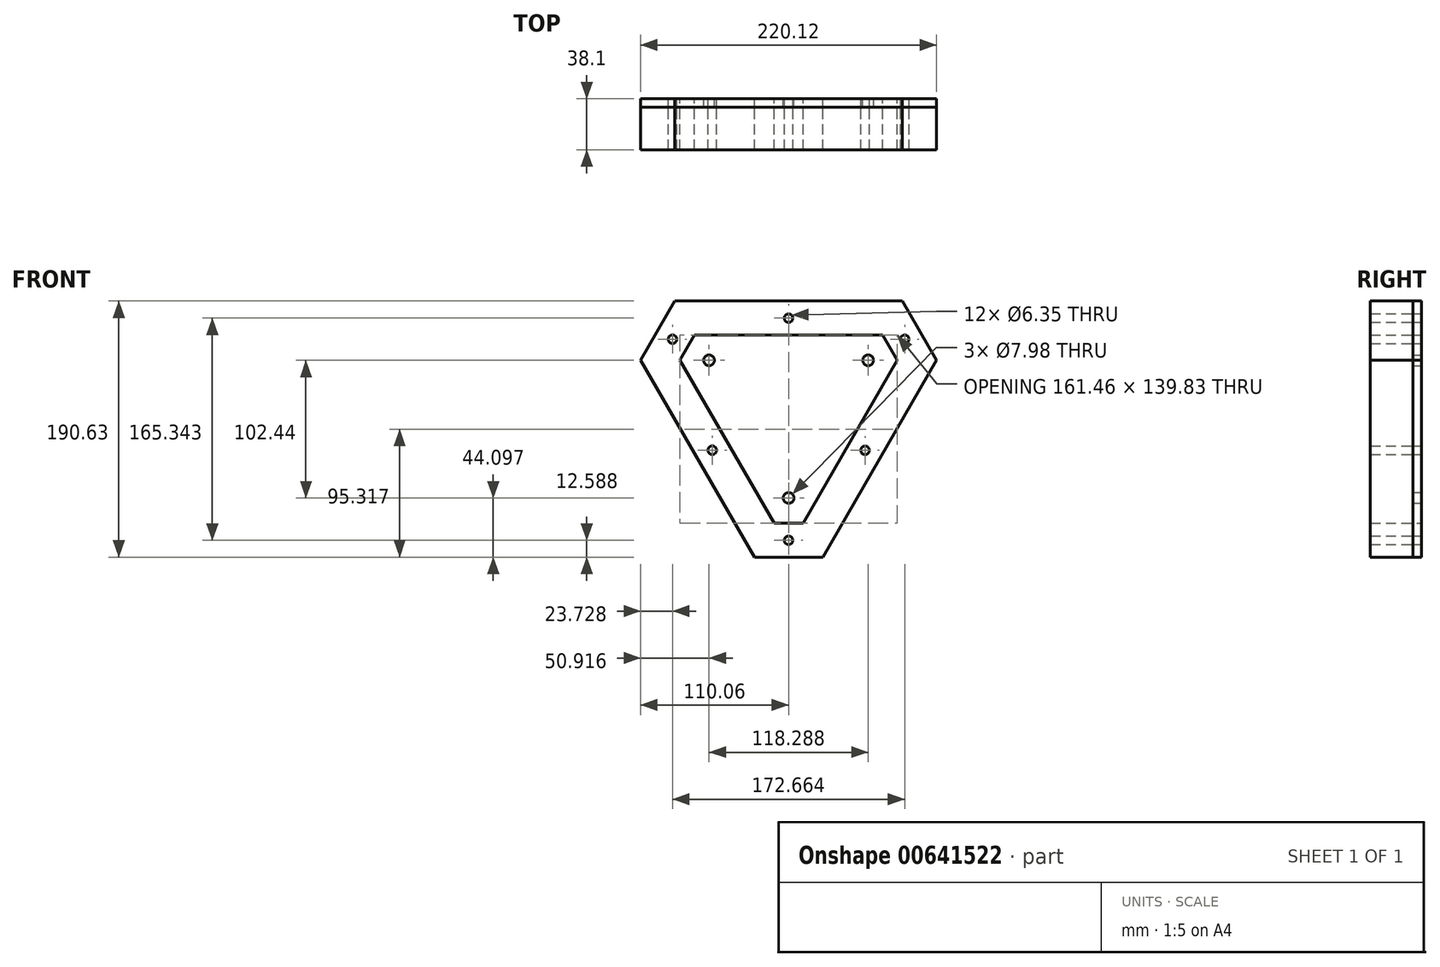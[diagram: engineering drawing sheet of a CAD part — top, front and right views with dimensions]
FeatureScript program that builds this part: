
annotation { "Feature Type Name" : "Feature", "Feature Type Description" : "" }
export const myFeature = defineFeature(function(context is Context, id is Id, definition is map)
    precondition{}
    {
        {
            var Q0;
            Q0=qCreatedBy(makeId("Front.planeOp"),FACE);
            var sketch = newSketch(context, id + "F0", { "sketchPlane" : qUnion([Q0])});
            skCircle(sketch, "E0.cCircle", {"center": v(0, 0) * mm, "radius": 68.3 * mm, "construction": true});
            skLineSegment(sketch, "E0.0", {"start": v(59.14, 34.15) * mm, "end": v(0, -68.3) * mm, "construction": true});
            skLineSegment(sketch, "E0.1", {"start": v(0, -68.3) * mm, "end": v(-59.14, 34.15) * mm, "construction": true});
            skLineSegment(sketch, "E0.2", {"start": v(-59.14, 34.15) * mm, "end": v(59.14, 34.15) * mm, "construction": true});
            skArc(sketch, "E1", {"start": v(-61.91, 28.83) * mm, "mid": v(-53.95, 31.15) * mm, "end": v(-55.92, 39.2) * mm, "construction": true});
            skArc(sketch, "E2", {"start": v(55.92, 39.2) * mm, "mid": v(53.95, 31.15) * mm, "end": v(61.91, 28.83) * mm, "construction": true});
            skArc(sketch, "E3", {"start": v(-5.2, -71.3) * mm, "mid": v(0, -74.29) * mm, "end": v(5.2, -71.3) * mm});
            skLineSegment(sketch, "E4", {"start": v(-59.14, 40.14) * mm, "end": v(59.14, 40.14) * mm});
            skLineSegment(sketch, "E5", {"start": v(64.34, 31.15) * mm, "end": v(5.2, -71.3) * mm});
            skLineSegment(sketch, "E6", {"start": v(-64.34, 31.15) * mm, "end": v(-5.2, -71.3) * mm});
            skArc(sketch, "E7.trimOffspring", {"start": v(-59.14, 40.14) * mm, "mid": v(-64.34, 37.14) * mm, "end": v(-64.34, 31.15) * mm});
            skArc(sketch, "E8.trimOffspring", {"start": v(64.34, 31.15) * mm, "mid": v(64.34, 37.14) * mm, "end": v(59.14, 40.14) * mm});
            skArc(sketch, "E9.trimOffspring", {"start": v(5.99, -68.03) * mm, "mid": v(0, -62.3) * mm, "end": v(-5.99, -68.03) * mm, "construction": true});
            skLineSegment(sketch, "E10", {"start": v(-69.94, 52.84) * mm, "end": v(69.94, 52.84) * mm});
            skLineSegment(sketch, "E11", {"start": v(80.73, 34.15) * mm, "end": v(69.94, 52.84) * mm});
            skLineSegment(sketch, "E12", {"start": v(10.8, -86.99) * mm, "end": v(-10.8, -86.99) * mm});
            skLineSegment(sketch, "E13", {"start": v(-10.8, -86.99) * mm, "end": v(-80.73, 34.15) * mm});
            skLineSegment(sketch, "E14", {"start": v(-69.94, 52.84) * mm, "end": v(-80.73, 34.15) * mm});
            skLineSegment(sketch, "E15", {"start": v(10.8, -86.99) * mm, "end": v(80.73, 34.15) * mm});
            skLineSegment(sketch, "E16", {"start": v(0, 52.84) * mm, "end": v(0, 78.24) * mm, "construction": true});
            skPoint(sketch, "E16.endSnap0", {"position": v(0, 52.84) * mm});
            skLineSegment(sketch, "E17", {"start": v(-45.76, -26.42) * mm, "end": v(-67.76, -39.12) * mm, "construction": true});
            skLineSegment(sketch, "E18", {"start": v(45.76, -26.42) * mm, "end": v(67.76, -39.12) * mm, "construction": true});
            skLineSegment(sketch, "E19", {"start": v(67.76, -39.12) * mm, "end": v(110.06, 34.15) * mm, "construction": true});
            skLineSegment(sketch, "E20", {"start": v(-110.06, 34.15) * mm, "end": v(-25.2, -112.39) * mm, "construction": true});
            skLineSegment(sketch, "E21", {"start": v(-84.6, 78.24) * mm, "end": v(84.6, 78.24) * mm, "construction": true});
            skLineSegment(sketch, "E22", {"start": v(67.76, -39.12) * mm, "end": v(25.46, -112.39) * mm, "construction": true});
            skLineSegment(sketch, "E23", {"start": v(0, -86.99) * mm, "end": v(0, -112.39) * mm, "construction": true});
            skLineSegment(sketch, "E24", {"start": v(0, -112.39) * mm, "end": v(-25.2, -112.39) * mm, "construction": true});
            skLineSegment(sketch, "E25", {"start": v(0, -112.39) * mm, "end": v(25.46, -112.39) * mm, "construction": true});
            skLineSegment(sketch, "E26", {"start": v(-25.2, -112.39) * mm, "end": v(-10.8, -86.99) * mm, "construction": true});
            skLineSegment(sketch, "E27", {"start": v(25.46, -112.39) * mm, "end": v(10.8, -86.99) * mm, "construction": true});
            skLineSegment(sketch, "E28", {"start": v(-75.33, 43.5) * mm, "end": v(-97.33, 56.2) * mm, "construction": true});
            skLineSegment(sketch, "E29", {"start": v(-97.33, 56.2) * mm, "end": v(-110.06, 34.15) * mm, "construction": true});
            skLineSegment(sketch, "E30", {"start": v(-97.33, 56.2) * mm, "end": v(-84.6, 78.24) * mm, "construction": true});
            skLineSegment(sketch, "E31", {"start": v(-80.73, 34.15) * mm, "end": v(-110.06, 34.15) * mm, "construction": true});
            skLineSegment(sketch, "E32", {"start": v(-69.94, 52.84) * mm, "end": v(-84.6, 78.24) * mm, "construction": true});
            skLineSegment(sketch, "E33", {"start": v(75.33, 43.5) * mm, "end": v(97.33, 56.2) * mm, "construction": true});
            skLineSegment(sketch, "E34", {"start": v(97.33, 56.2) * mm, "end": v(84.6, 78.24) * mm, "construction": true});
            skLineSegment(sketch, "E35", {"start": v(97.33, 56.2) * mm, "end": v(110.06, 34.15) * mm, "construction": true});
            skLineSegment(sketch, "E36", {"start": v(69.94, 52.84) * mm, "end": v(84.6, 78.24) * mm, "construction": true});
            skLineSegment(sketch, "E37", {"start": v(80.73, 34.15) * mm, "end": v(110.06, 34.15) * mm, "construction": true});
            skLineSegment(sketch, "E38", {"start": v(-110.06, 34.15) * mm, "end": v(-110.06, 78.24) * mm, "construction": true});
            skLineSegment(sketch, "E39", {"start": v(-110.06, 34.15) * mm, "end": v(-110.06, -112.39) * mm, "construction": true});
            skLineSegment(sketch, "E40", {"start": v(-84.6, 78.24) * mm, "end": v(-110.06, 78.24) * mm, "construction": true});
            skLineSegment(sketch, "E41", {"start": v(-25.2, -112.39) * mm, "end": v(-110.06, -112.39) * mm, "construction": true});
            skLineSegment(sketch, "E42", {"start": v(110.06, 34.15) * mm, "end": v(110.06, 78.24) * mm, "construction": true});
            skLineSegment(sketch, "E43", {"start": v(84.6, 78.24) * mm, "end": v(110.06, 78.24) * mm, "construction": true});
            skLineSegment(sketch, "E44", {"start": v(110.06, 34.15) * mm, "end": v(110.06, -112.39) * mm, "construction": true});
            skLineSegment(sketch, "E45", {"start": v(25.46, -112.39) * mm, "end": v(110.06, -112.39) * mm, "construction": true});
            skLineSegment(sketch, "E46", {"start": v(-110.06, 78.24) * mm, "end": v(110.06, 78.24) * mm});
            skLineSegment(sketch, "E47", {"start": v(110.06, -112.39) * mm, "end": v(110.06, 78.24) * mm});
            skLineSegment(sketch, "E48", {"start": v(110.06, -112.39) * mm, "end": v(-110.06, -112.39) * mm});
            skLineSegment(sketch, "E49", {"start": v(-110.06, -112.39) * mm, "end": v(-110.06, 78.24) * mm});
            skCircle(sketch, "E50", {"center": v(0, -68.3) * mm, "radius": 3.99 * mm});
            skCircle(sketch, "E51", {"center": v(59.14, 34.15) * mm, "radius": 3.99 * mm});
            skCircle(sketch, "E52", {"center": v(-59.14, 34.15) * mm, "radius": 3.99 * mm});
            skLineSegment(sketch, "E53", {"start": v(-84.6, 78.24) * mm, "end": v(-110.06, 34.15) * mm});
            skLineSegment(sketch, "E54", {"start": v(-110.06, 34.15) * mm, "end": v(-25.2, -112.39) * mm});
            skLineSegment(sketch, "E55", {"start": v(25.46, -112.39) * mm, "end": v(110.06, 34.15) * mm});
            skLineSegment(sketch, "E56", {"start": v(110.06, 34.15) * mm, "end": v(84.6, 78.24) * mm});
            skLineSegment(sketch, "E57", {"start": v(25.46, -112.39) * mm, "end": v(10.8, -86.99) * mm});
            skLineSegment(sketch, "E58", {"start": v(-10.8, -86.99) * mm, "end": v(-25.2, -112.39) * mm});
            skLineSegment(sketch, "E59", {"start": v(80.73, 34.15) * mm, "end": v(110.06, 34.15) * mm});
            skLineSegment(sketch, "E60", {"start": v(69.94, 52.84) * mm, "end": v(84.6, 78.24) * mm});
            skLineSegment(sketch, "E61", {"start": v(-69.94, 52.84) * mm, "end": v(-84.6, 78.24) * mm});
            skLineSegment(sketch, "E62", {"start": v(-80.73, 34.15) * mm, "end": v(-110.06, 34.15) * mm});
            skLineSegment(sketch, "E63", {"start": v(0, 65.54) * mm, "end": v(-77.27, 65.54) * mm, "construction": true});
            skLineSegment(sketch, "E64", {"start": v(-77.27, 65.54) * mm, "end": v(-95.4, 34.15) * mm, "construction": true});
            skLineSegment(sketch, "E65", {"start": v(-95.4, 34.15) * mm, "end": v(-56.76, -32.77) * mm, "construction": true});
            skLineSegment(sketch, "E66", {"start": v(-56.76, -32.77) * mm, "end": v(-18.06, -99.8) * mm, "construction": true});
            skLineSegment(sketch, "E67", {"start": v(-18.06, -99.8) * mm, "end": v(18.2, -99.8) * mm, "construction": true});
            skLineSegment(sketch, "E68", {"start": v(18.2, -99.8) * mm, "end": v(56.86, -32.83) * mm, "construction": true});
            skLineSegment(sketch, "E69", {"start": v(56.86, -32.83) * mm, "end": v(94.84, 34.15) * mm, "construction": true});
            skPoint(sketch, "E70.endSnap0", {"position": v(77.27, 65.54) * mm});
            skLineSegment(sketch, "E71", {"start": v(77.27, 65.54) * mm, "end": v(0, 65.54) * mm, "construction": true});
            skLineSegment(sketch, "E72", {"start": v(77.27, 65.54) * mm, "end": v(86.33, 49.84) * mm, "construction": true});
            skLineSegment(sketch, "E73", {"start": v(86.33, 49.84) * mm, "end": v(94.84, 34.15) * mm, "construction": true});
            skCircle(sketch, "E74", {"center": v(-56.76, -32.77) * mm, "radius": 3.18 * mm});
            skCircle(sketch, "E75", {"center": v(56.86, -32.83) * mm, "radius": 3.18 * mm});
            skCircle(sketch, "E76", {"center": v(0, -99.8) * mm, "radius": 3.18 * mm});
            skCircle(sketch, "E77", {"center": v(0, 65.54) * mm, "radius": 3.18 * mm});
            skCircle(sketch, "E78", {"center": v(-86.33, 49.84) * mm, "radius": 3.18 * mm});
            skCircle(sketch, "E79", {"center": v(86.33, 49.84) * mm, "radius": 3.18 * mm});
            skSolve(sketch);
        }
        {
            var Q0;
            Q0=makeQuery(id+"F0.imprint","IMPRINT",FACE,{"disambiguationData":[TD([[makeQuery(id+"F0.imprint","IMPRINT",EDGE,{"derivedFrom":sQuery(id+"F0.wireOp",EDGE,"E3")}),-1.0]])]});
            var Q1;
            Q1=makeQuery(id+"F0.imprint","IMPRINT",FACE,{"disambiguationData":[TD([[makeQuery(id+"F0.imprint","IMPRINT",EDGE,{"derivedFrom":sQuery(id+"F0.wireOp",EDGE,"E3")}),1.0]])]});
            var Q2;
            Q2=makeQuery(id+"F0.imprint","IMPRINT",FACE,{"disambiguationData":[TD([[makeQuery(id+"F0.imprint","IMPRINT",EDGE,{"derivedFrom":sQuery(id+"F0.wireOp",EDGE,"E14")}),-1.0]])]});
            var Q3;
            Q3=makeQuery(id+"F0.imprint","IMPRINT",FACE,{"disambiguationData":[TD([[makeQuery(id+"F0.imprint","IMPRINT",EDGE,{"derivedFrom":sQuery(id+"F0.wireOp",EDGE,"E13")}),1.0]])]});
            var Q4;
            Q4=makeQuery(id+"F0.imprint","IMPRINT",FACE,{"disambiguationData":[TD([[makeQuery(id+"F0.imprint","IMPRINT",EDGE,{"derivedFrom":sQuery(id+"F0.wireOp",EDGE,"E12")}),1.0]])]});
            var Q5;
            Q5=makeQuery(id+"F0.imprint","IMPRINT",FACE,{"disambiguationData":[TD([[makeQuery(id+"F0.imprint","IMPRINT",EDGE,{"derivedFrom":sQuery(id+"F0.wireOp",EDGE,"E15")}),-1.0]])]});
            var Q6;
            Q6=makeQuery(id+"F0.imprint","IMPRINT",FACE,{"disambiguationData":[TD([[makeQuery(id+"F0.imprint","IMPRINT",EDGE,{"derivedFrom":sQuery(id+"F0.wireOp",EDGE,"E11")}),-1.0]])]});
            var Q7;
            Q7=makeQuery(id+"F0.imprint","IMPRINT",FACE,{"disambiguationData":[TD([[makeQuery(id+"F0.imprint","IMPRINT",EDGE,{"derivedFrom":sQuery(id+"F0.wireOp",EDGE,"E10")}),1.0]])]});
            extrude(context, id + "F1", {"entities" : qUnion([Q0, Q1, Q2, Q3, Q4, Q5, Q6, Q7]), "depth" : 6.35 * mm, "offsetDistance" : 25.4 * mm});
        }
        {
            var Q0;
            Q0=makeQuery(id+"F0.imprint","IMPRINT",FACE,{"disambiguationData":[TD([[makeQuery(id+"F0.imprint","IMPRINT",EDGE,{"derivedFrom":sQuery(id+"F0.wireOp",EDGE,"E14")}),-1.0]])]});
            var Q1;
            Q1=makeQuery(id+"F0.imprint","IMPRINT",FACE,{"disambiguationData":[TD([[makeQuery(id+"F0.imprint","IMPRINT",EDGE,{"derivedFrom":sQuery(id+"F0.wireOp",EDGE,"E13")}),1.0]])]});
            var Q2;
            Q2=makeQuery(id+"F0.imprint","IMPRINT",FACE,{"disambiguationData":[TD([[makeQuery(id+"F0.imprint","IMPRINT",EDGE,{"derivedFrom":sQuery(id+"F0.wireOp",EDGE,"E12")}),1.0]])]});
            var Q3;
            Q3=makeQuery(id+"F0.imprint","IMPRINT",FACE,{"disambiguationData":[TD([[makeQuery(id+"F0.imprint","IMPRINT",EDGE,{"derivedFrom":sQuery(id+"F0.wireOp",EDGE,"E15")}),-1.0]])]});
            var Q4;
            Q4=makeQuery(id+"F0.imprint","IMPRINT",FACE,{"disambiguationData":[TD([[makeQuery(id+"F0.imprint","IMPRINT",EDGE,{"derivedFrom":sQuery(id+"F0.wireOp",EDGE,"E11")}),-1.0]])]});
            var Q5;
            Q5=makeQuery(id+"F0.imprint","IMPRINT",FACE,{"disambiguationData":[TD([[makeQuery(id+"F0.imprint","IMPRINT",EDGE,{"derivedFrom":sQuery(id+"F0.wireOp",EDGE,"E10")}),1.0]])]});
            extrude(context, id + "F2", {"entities" : qUnion([Q0, Q1, Q2, Q3, Q4, Q5]), "depth" : 38.1 * mm, "offsetDistance" : 25.4 * mm});
        }
    });
